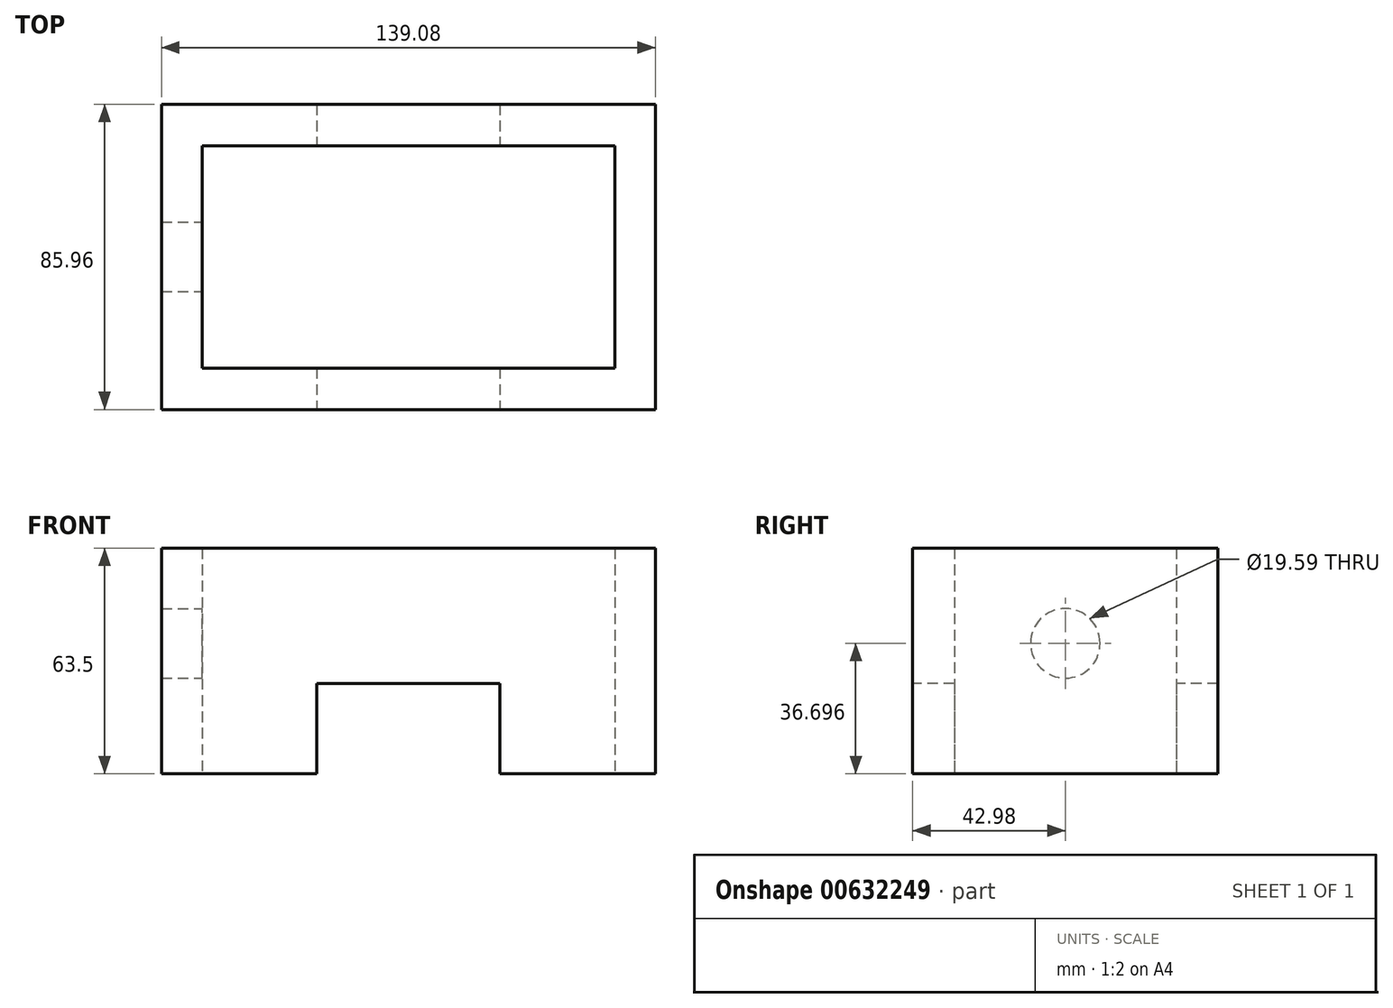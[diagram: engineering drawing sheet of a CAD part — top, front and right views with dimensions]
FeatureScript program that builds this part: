
annotation { "Feature Type Name" : "Feature", "Feature Type Description" : "" }
export const myFeature = defineFeature(function(context is Context, id is Id, definition is map)
    precondition{}
    {
        {
            var Q0;
            Q0=qCreatedBy(makeId("Top.planeOp"),FACE);
            var sketch = newSketch(context, id + "F0", { "sketchPlane" : qUnion([Q0])});
            skLineSegment(sketch, "E0.bottom", {"start": v(-69.54, 42.98) * mm, "end": v(69.54, 42.98) * mm});
            skLineSegment(sketch, "E0.top", {"start": v(-69.54, -42.98) * mm, "end": v(69.54, -42.98) * mm});
            skLineSegment(sketch, "E0.left", {"start": v(-69.54, 42.98) * mm, "end": v(-69.54, -42.98) * mm});
            skLineSegment(sketch, "E0.right", {"start": v(69.54, 42.98) * mm, "end": v(69.54, -42.98) * mm});
            skPoint(sketch, "E0.middle", {"position": v(0, 0) * mm});
            skLineSegment(sketch, "E1.bottom", {"start": v(-58.11, 31.27) * mm, "end": v(58.11, 31.27) * mm});
            skLineSegment(sketch, "E1.top", {"start": v(-58.11, -31.27) * mm, "end": v(58.11, -31.27) * mm});
            skLineSegment(sketch, "E1.left", {"start": v(-58.11, 31.27) * mm, "end": v(-58.11, -31.27) * mm});
            skLineSegment(sketch, "E1.right", {"start": v(58.11, 31.27) * mm, "end": v(58.11, -31.27) * mm});
            skSolve(sketch);
        }
        {
            var Q0;
            Q0 = qSketchRegion(id + "F0", true);
            extrude(context, id + "F1", {"entities" : qUnion([Q0]), "depth" : 63.5 * mm, "offsetDistance" : 25.4 * mm});
        }
        {
            var Q0;
            Q0=qCreatedBy(makeId("Top.planeOp"),FACE);
            var sketch = newSketch(context, id + "F2", { "sketchPlane" : qUnion([Q0])});
            skLineSegment(sketch, "E2.bottom", {"start": v(-25.74, 50.73) * mm, "end": v(25.74, 50.73) * mm});
            skLineSegment(sketch, "E2.top", {"start": v(-25.74, -50.73) * mm, "end": v(25.74, -50.73) * mm});
            skLineSegment(sketch, "E2.left", {"start": v(-25.74, 50.73) * mm, "end": v(-25.74, -50.73) * mm});
            skLineSegment(sketch, "E2.right", {"start": v(25.74, 50.73) * mm, "end": v(25.74, -50.73) * mm});
            skPoint(sketch, "E2.middle", {"position": v(0, 0) * mm});
            skSolve(sketch);
        }
        {
            var Q0;
            Q0 = qSketchRegion(id + "F2", true);
            extrude(context, id + "F3", {"entities" : qUnion([Q0]), "operationType" : NewBodyOperationType.ADD, "depth" : 25.4 * mm, "offsetDistance" : 25.4 * mm});
        }
        {
            var Q0;
            Q0=makeQuery(id+"F2.imprint","IMPRINT",FACE,{"disambiguationData":[TD([[makeQuery(id+"F2.imprint","IMPRINT",EDGE,{"derivedFrom":sQuery(id+"F2.wireOp",EDGE,"E2.bottom")}),-1.0]])]});
            extrude(context, id + "F4", {"entities" : qUnion([Q0]), "operationType" : NewBodyOperationType.REMOVE, "depth" : 25.4 * mm, "offsetDistance" : 25.4 * mm});
        }
        {
            var Q0;
            Q0=qCreatedBy(makeId("Right.planeOp"),FACE);
            var sketch = newSketch(context, id + "F5", { "sketchPlane" : qUnion([Q0])});
            skCircle(sketch, "E3", {"center": v(0, 36.7) * mm, "radius": 9.8 * mm});
            skSolve(sketch);
        }
        {
            var Q0;
            Q0 = qSketchRegion(id + "F5", true);
            extrude(context, id + "F6", {"entities" : qUnion([Q0]), "operationType" : NewBodyOperationType.REMOVE, "endBound" : BoundingType.THROUGH_ALL, "oppositeDirection" : true, "depth" : 127 * mm, "offsetDistance" : 25.4 * mm});
        }
    });
